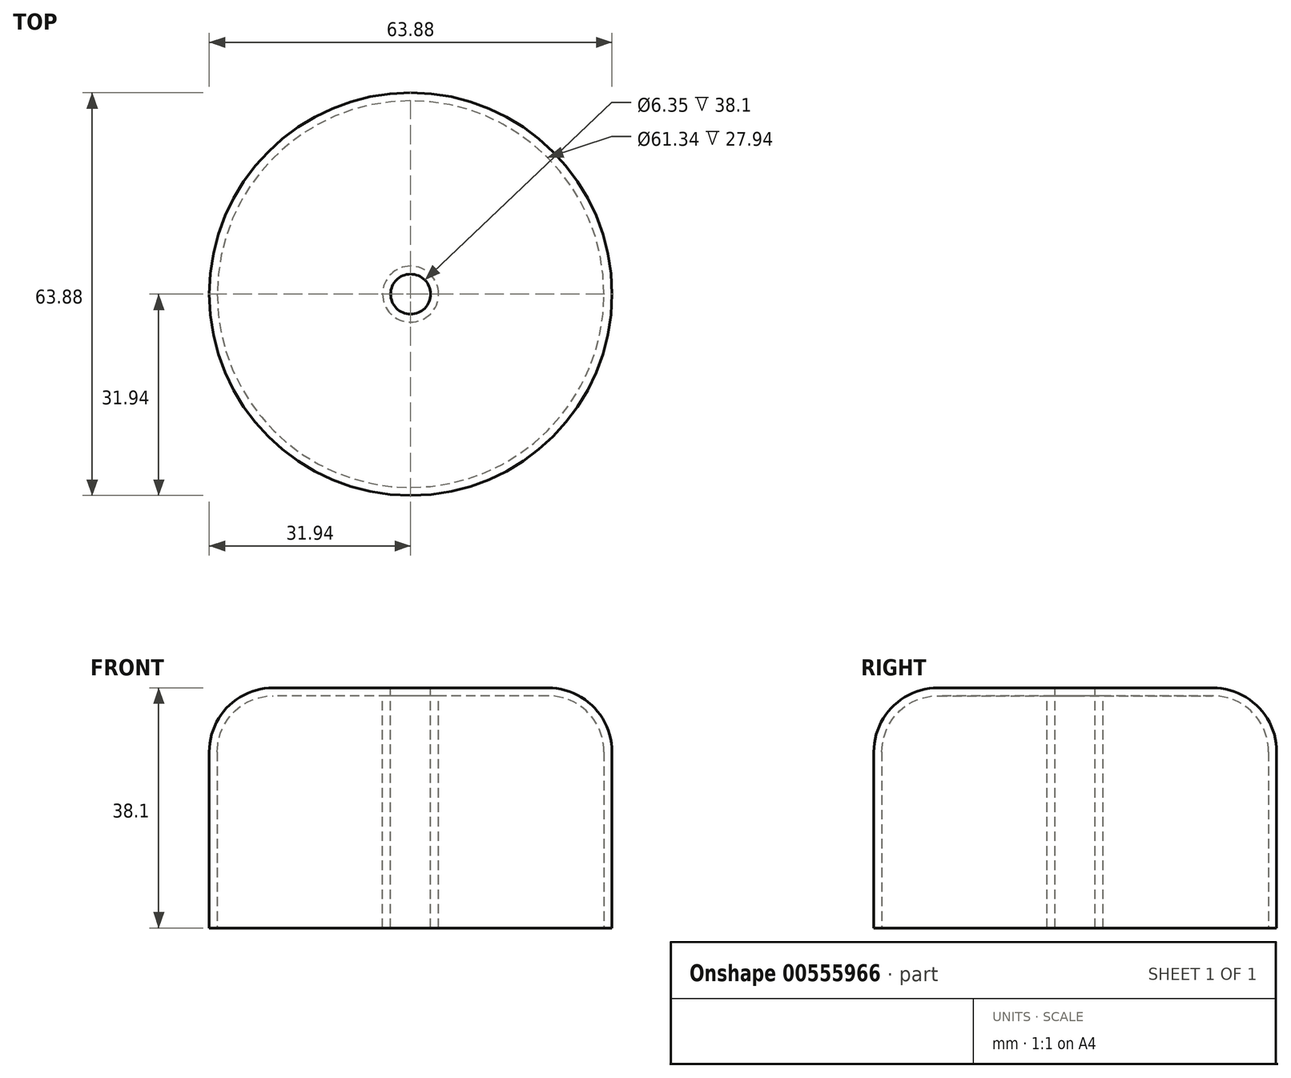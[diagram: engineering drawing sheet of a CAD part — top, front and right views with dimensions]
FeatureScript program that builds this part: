
annotation { "Feature Type Name" : "Feature", "Feature Type Description" : "" }
export const myFeature = defineFeature(function(context is Context, id is Id, definition is map)
    precondition{}
    {
        {
            var Q0;
            Q0=qCreatedBy(makeId("Top.planeOp"),FACE);
            var sketch = newSketch(context, id + "F0", { "sketchPlane" : qUnion([Q0])});
            skCircle(sketch, "E0", {"center": v(0, 0) * mm, "radius": 31.94 * mm});
            skSolve(sketch);
        }
        {
            var Q0;
            Q0 = qSketchRegion(id + "F0", true);
            extrude(context, id + "F1", {"entities" : qUnion([Q0]), "depth" : 38.1 * mm, "offsetDistance" : 25.4 * mm});
        }
        {
            var Q0;
            Q0=makeQuery(id+"F1.opExtrude","CAP_EDGE",EDGE,{"disambiguationData":[OSD([sQuery(id+"F0.wireOp",EDGE,"E0")])],"isStart":false});
            fillet(context, id + "F2", {"entities" : qUnion([Q0]), "radius" : 10.16 * mm, "tangentPropagation" : true, "allowEdgeOverflow" : false});
        }
        {
            var Q0;
            Q0=makeQuery(id+"F1.opExtrude","CAP_FACE",FACE,{"disambiguationData":[OSD([sQuery(id+"F0.wireOp",EDGE,"E0")])],"isStart":false});
            var sketch = newSketch(context, id + "F3", { "sketchPlane" : qUnion([Q0])});
            skCircle(sketch, "E1", {"center": v(0, 0) * mm, "radius": 6.42 * mm});
            skSolve(sketch);
        }
        {
            var Q0;
            Q0=sQuery(id+"F3.wireOp",VERTEX,"E1.center");
            var Q1;
            Q1=makeQuery(id+"F1.opExtrude","SWEPT_BODY",BODY,{"disambiguationData":[OSD([sQuery(id+"F0.wireOp",EDGE,"E0")])]});
            hole(context, id + "F4", {"style" : HoleStyle.SIMPLE, "endStyle" : HoleEndStyle.THROUGH, "holeDiameter" : 6.35 * mm, "isTappedThrough" : true, "tappedDepth" : 12.7 * mm, "tapClearance" : 3, "locations" : qUnion([Q0]), "scope" : qUnion([Q1])});
        }
        {
            var Q0;
            Q0=makeQuery(id+"F1.opExtrude","CAP_FACE",FACE,{"disambiguationData":[OSD([sQuery(id+"F0.wireOp",EDGE,"E0")])],"isStart":true});
            shell(context, id + "F5", {"entities" : qUnion([Q0]), "thickness" : 1.27 * mm});
        }
    });
